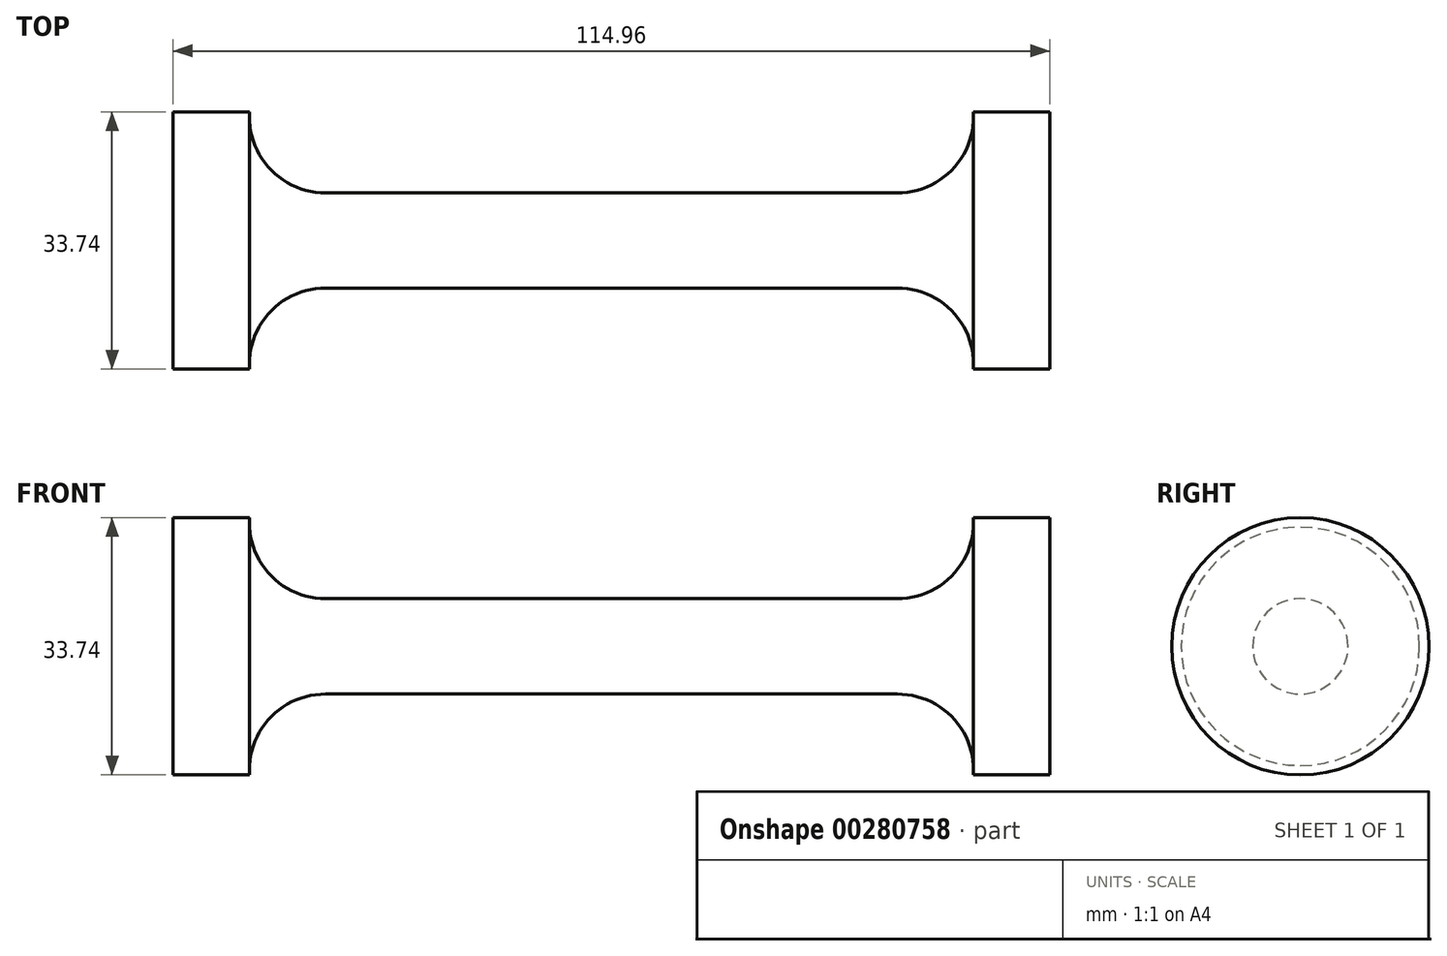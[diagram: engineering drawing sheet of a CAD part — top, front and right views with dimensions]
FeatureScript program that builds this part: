
annotation { "Feature Type Name" : "Feature", "Feature Type Description" : "" }
export const myFeature = defineFeature(function(context is Context, id is Id, definition is map)
    precondition{}
    {
        {
            var Q0;
            Q0=qCreatedBy(makeId("Front.planeOp"),FACE);
            var sketch = newSketch(context, id + "F0", { "sketchPlane" : qUnion([Q0])});
            skLineSegment(sketch, "E0", {"start": v(0, 6.25) * mm, "end": v(37.5, 6.25) * mm});
            skArc(sketch, "E1", {"start": v(37.5, 6.25) * mm, "mid": v(44.79, 9.4) * mm, "end": v(47.48, 16.87) * mm});
            skLineSegment(sketch, "E2", {"start": v(47.48, 16.87) * mm, "end": v(47.48, 0) * mm});
            skLineSegment(sketch, "E3.MirrorCS", {"start": v(0, 6.25) * mm, "end": v(-37.5, 6.25) * mm});
            skArc(sketch, "E4.MirrorCS", {"start": v(-37.5, 6.25) * mm, "mid": v(-44.79, 9.4) * mm, "end": v(-47.48, 16.87) * mm});
            skLineSegment(sketch, "E5.MirrorCS", {"start": v(-47.48, 16.87) * mm, "end": v(-47.48, 0) * mm});
            skLineSegment(sketch, "E6", {"start": v(47.48, 16.87) * mm, "end": v(57.48, 16.87) * mm});
            skLineSegment(sketch, "E7", {"start": v(-47.48, 16.87) * mm, "end": v(-64.36, 16.87) * mm});
            skLineSegment(sketch, "E8", {"start": v(-57.48, 0) * mm, "end": v(57.48, 0) * mm});
            skLineSegment(sketch, "E9", {"start": v(57.48, 16.87) * mm, "end": v(57.48, 0) * mm});
            skLineSegment(sketch, "E10", {"start": v(-57.48, 0) * mm, "end": v(-57.48, 16.87) * mm});
            skSolve(sketch);
        }
        {
            var Q0;
            Q0 = qSketchRegion(id + "F0", true);
            var Q1;
            Q1=sQuery(id+"F0.wireOp",EDGE,"E8");
            revolve(context, id + "F1", {"entities" : qUnion([Q0]), "axis" : qUnion([Q1]), "revolveType" : RevolveType.FULL});
        }
    });
